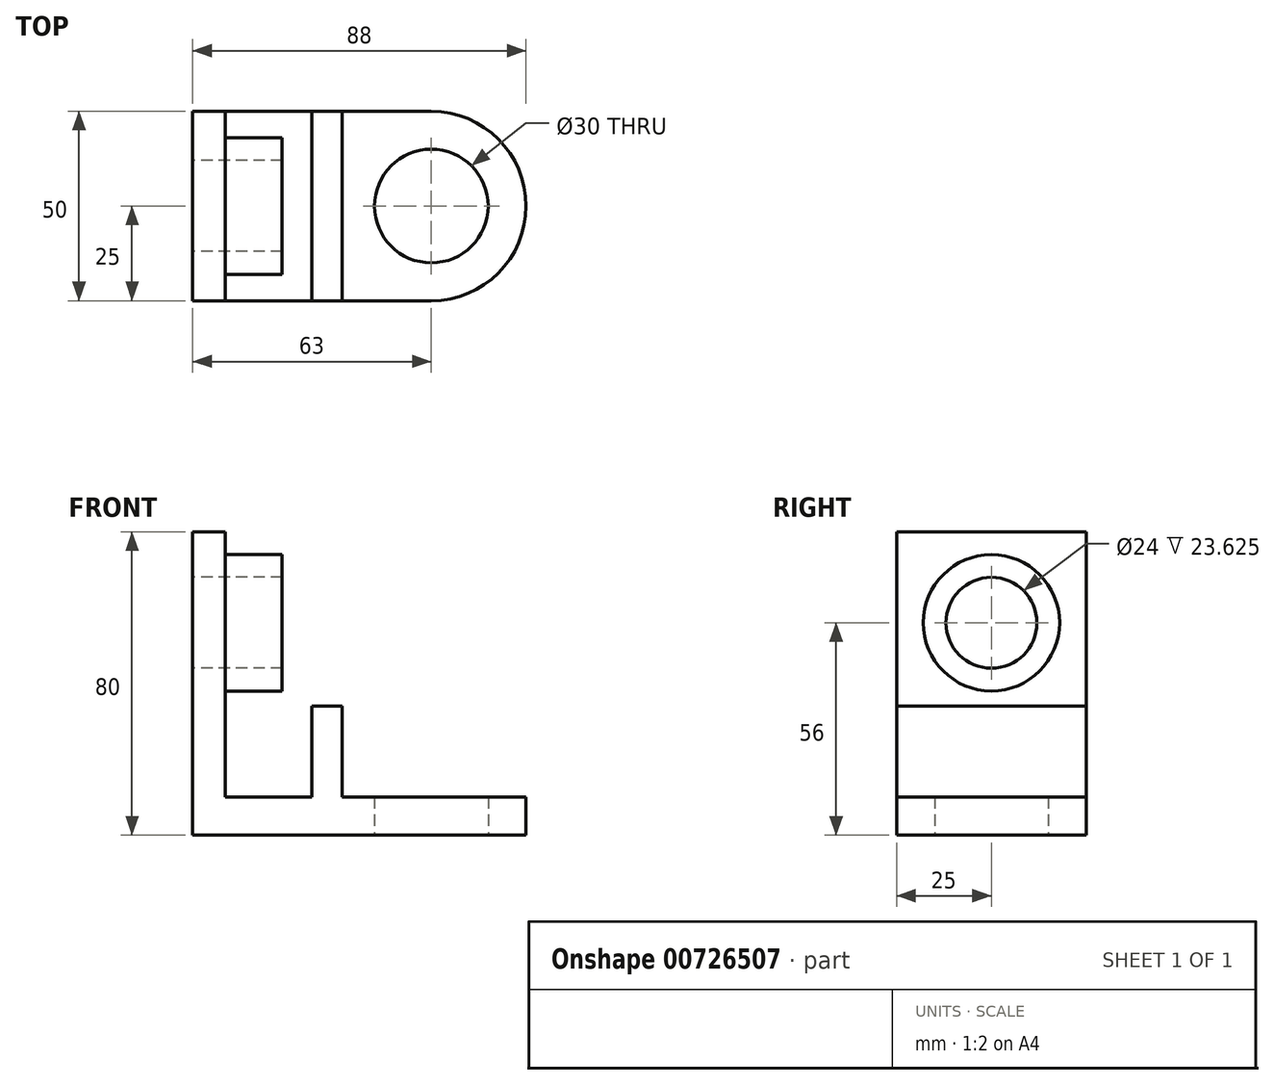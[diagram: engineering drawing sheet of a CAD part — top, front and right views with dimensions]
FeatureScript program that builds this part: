
annotation { "Feature Type Name" : "Feature", "Feature Type Description" : "" }
export const myFeature = defineFeature(function(context is Context, id is Id, definition is map)
    precondition{}
    {
        {
            var Q0;
            Q0=qCreatedBy(makeId("Top.planeOp"),FACE);
            var sketch = newSketch(context, id + "F0", { "sketchPlane" : qUnion([Q0])});
            skLineSegment(sketch, "E0.bottom", {"start": v(0, 0) * mm, "end": v(63, 0) * mm});
            skLineSegment(sketch, "E0.top", {"start": v(0, 50) * mm, "end": v(63, 50) * mm});
            skLineSegment(sketch, "E0.left", {"start": v(0, 0) * mm, "end": v(0, 50) * mm});
            skLineSegment(sketch, "E0.right", {"start": v(63, 40) * mm, "end": v(63, 50) * mm});
            skCircle(sketch, "E1", {"center": v(63, 25) * mm, "radius": 15 * mm});
            skArc(sketch, "E2", {"start": v(63, 0) * mm, "mid": v(88, 25) * mm, "end": v(63, 50) * mm});
            skSolve(sketch);
        }
        {
            var Q0;
            Q0 = qSketchRegion(id + "F0", true);
            extrude(context, id + "F1", {"entities" : qUnion([Q0]), "depth" : 10 * mm, "offsetDistance" : 25 * mm});
        }
        {
            var Q0;
            Q0=makeQuery(id+"F1.opExtrude","CAP_FACE",FACE,{"disambiguationData":[OSD([sQuery(id+"F0.wireOp",EDGE,"E0.bottom"),sQuery(id+"F0.wireOp",EDGE,"E0.top"),sQuery(id+"F0.wireOp",EDGE,"E0.left"),sQuery(id+"F0.wireOp",EDGE,"E1"),sQuery(id+"F0.wireOp",EDGE,"E2")])],"isStart":false});
            var sketch = newSketch(context, id + "F2", { "sketchPlane" : qUnion([Q0])});
            skLineSegment(sketch, "E3.bottom", {"start": v(31.5, 0) * mm, "end": v(31.5, 0) * mm});
            skLineSegment(sketch, "E3.top", {"start": v(31.5, 50) * mm, "end": v(31.5, 50) * mm});
            skLineSegment(sketch, "E4.bottom", {"start": v(31.5, 25) * mm, "end": v(31.5, 25) * mm});
            skLineSegment(sketch, "E4.top", {"start": v(31.5, 40.73) * mm, "end": v(31.5, 40.73) * mm});
            skLineSegment(sketch, "E5.bottom", {"start": v(31.5, 0) * mm, "end": v(39.5, 0) * mm});
            skLineSegment(sketch, "E5.top", {"start": v(31.5, 50) * mm, "end": v(39.5, 50) * mm});
            skLineSegment(sketch, "E5.left", {"start": v(31.5, 0) * mm, "end": v(31.5, 50) * mm});
            skLineSegment(sketch, "E5.right", {"start": v(39.5, 0) * mm, "end": v(39.5, 50) * mm});
            skSolve(sketch);
        }
        {
            var Q0;
            Q0 = qSketchRegion(id + "F2", true);
            extrude(context, id + "F3", {"entities" : qUnion([Q0]), "operationType" : NewBodyOperationType.ADD, "depth" : 24 * mm, "offsetDistance" : 25 * mm});
        }
        {
            var Q0;
            {var subQ0=sQuery(id+"F0.wireOp",EDGE,"E0.left");var subQ1=sQuery(id+"F0.wireOp",EDGE,"E0.top");var subQ2=sQuery(id+"F0.wireOp",EDGE,"E0.bottom");Q0=makeQuery(id+"F3.boolean.opBoolean","SPLIT",FACE,{"disambiguationData":[TD([makeQuery(id+"F1.opExtrude","SWEPT_FACE",FACE,{"disambiguationData":[OSD([subQ0])]})])],"derivedFrom":makeQuery(id+"F1.opExtrude","CAP_FACE",FACE,{"disambiguationData":[OSD([subQ2,subQ1,subQ0,sQuery(id+"F0.wireOp",EDGE,"E1"),sQuery(id+"F0.wireOp",EDGE,"E2")])],"isStart":false})});}
            var sketch = newSketch(context, id + "F4", { "sketchPlane" : qUnion([Q0])});
            skLineSegment(sketch, "E6.bottom", {"start": v(0, 0) * mm, "end": v(8.62, 0) * mm});
            skLineSegment(sketch, "E6.top", {"start": v(0, 50) * mm, "end": v(8.62, 50) * mm});
            skLineSegment(sketch, "E6.left", {"start": v(0, 0) * mm, "end": v(0, 50) * mm});
            skLineSegment(sketch, "E6.right", {"start": v(8.62, 0) * mm, "end": v(8.62, 50) * mm});
            skSolve(sketch);
        }
        {
            var Q0;
            Q0=makeQuery(id+"F4.imprint","IMPRINT",FACE,{"disambiguationData":[TD([[makeQuery(id+"F4.imprint","IMPRINT",EDGE,{"derivedFrom":sQuery(id+"F4.wireOp",EDGE,"E6.bottom")}),1.0]])]});
            extrude(context, id + "F5", {"entities" : qUnion([Q0]), "operationType" : NewBodyOperationType.ADD, "depth" : 70 * mm, "offsetDistance" : 25 * mm});
        }
        {
            var Q0;
            Q0=makeQuery(id+"F5.opExtrude","SWEPT_FACE",FACE,{"disambiguationData":[OSD([sQuery(id+"F4.wireOp",EDGE,"E6.right")])]});
            var sketch = newSketch(context, id + "F6", { "sketchPlane" : qUnion([Q0])});
            skCircle(sketch, "E7", {"center": v(25, 56) * mm, "radius": 18 * mm});
            skCircle(sketch, "E8", {"center": v(25, 56) * mm, "radius": 12 * mm});
            skSolve(sketch);
        }
        {
            var Q0;
            Q0 = qSketchRegion(id + "F6", true);
            extrude(context, id + "F7", {"entities" : qUnion([Q0]), "operationType" : NewBodyOperationType.ADD, "depth" : 15 * mm, "offsetDistance" : 25 * mm});
        }
        {
            var Q0;
            Q0=makeQuery(id+"F7.boolean.opBoolean","SPLIT",FACE,{"disambiguationData":[TD([makeQuery(id+"F7.opExtrude","SWEPT_FACE",FACE,{"disambiguationData":[OSD([sQuery(id+"F6.wireOp",EDGE,"E8")])]})])],"derivedFrom":makeQuery(id+"F5.opExtrude","SWEPT_FACE",FACE,{"disambiguationData":[OSD([sQuery(id+"F4.wireOp",EDGE,"E6.right")])]})});
            var sketch = newSketch(context, id + "F8", { "sketchPlane" : qUnion([Q0])});
            skCircle(sketch, "E9", {"center": v(25, 56) * mm, "radius": 12 * mm});
            skSolve(sketch);
        }
        {
            var Q0;
            Q0 = qSketchRegion(id + "F8", true);
            extrude(context, id + "F9", {"entities" : qUnion([Q0]), "operationType" : NewBodyOperationType.REMOVE, "endBound" : BoundingType.UP_TO_NEXT, "oppositeDirection" : true, "depth" : 25 * mm, "offsetDistance" : 25 * mm});
        }
    });
